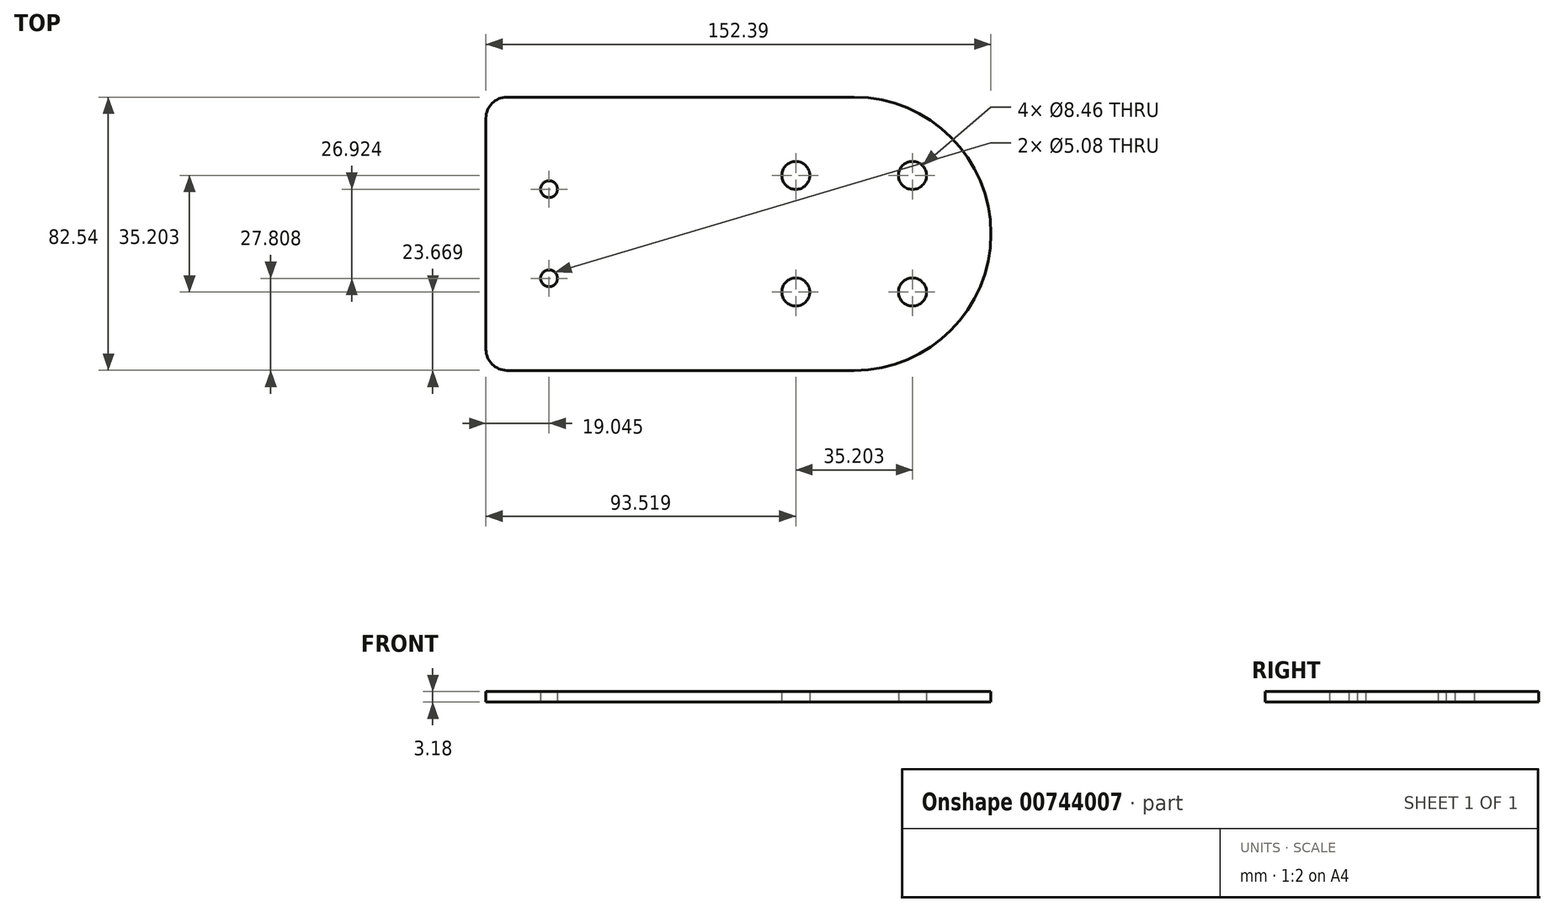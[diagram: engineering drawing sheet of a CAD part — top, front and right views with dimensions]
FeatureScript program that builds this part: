
annotation { "Feature Type Name" : "Feature", "Feature Type Description" : "" }
export const myFeature = defineFeature(function(context is Context, id is Id, definition is map)
    precondition{}
    {
        {
            var Q0;
            Q0=qCreatedBy(makeId("Top.planeOp"),FACE);
            var sketch = newSketch(context, id + "F0", { "sketchPlane" : qUnion([Q0])});
            skCircle(sketch, "E0", {"center": v(0, 0) * mm, "radius": 41.28 * mm});
            skLineSegment(sketch, "E1", {"start": v(-17.6, 17.6) * mm, "end": v(0, 0) * mm});
            skLineSegment(sketch, "E2", {"start": v(0, 2.83) * mm, "end": v(0, 41.28) * mm});
            skLineSegment(sketch, "E3.bottom", {"start": v(0, 41.28) * mm, "end": v(-104.78, 41.28) * mm});
            skLineSegment(sketch, "E3.top", {"start": v(0, -41.28) * mm, "end": v(-104.78, -41.28) * mm});
            skLineSegment(sketch, "E3.left", {"start": v(0, 41.28) * mm, "end": v(0, -41.28) * mm});
            skLineSegment(sketch, "E3.right", {"start": v(-111.13, 34.92) * mm, "end": v(-111.13, -34.92) * mm});
            skPoint(sketch, "E4.visualSharp", {"position": v(-111.13, -41.27) * mm});
            skArc(sketch, "E4.filletArc", {"start": v(-111.13, -34.92) * mm, "mid": v(-109.27, -39.42) * mm, "end": v(-104.78, -41.27) * mm});
            skPoint(sketch, "E5.visualSharp", {"position": v(-111.13, 41.27) * mm});
            skArc(sketch, "E5.filletArc", {"start": v(-104.78, 41.27) * mm, "mid": v(-109.27, 39.42) * mm, "end": v(-111.13, 34.92) * mm});
            skLineSegment(sketch, "E6", {"start": v(0, 0) * mm, "end": v(-111.13, 0) * mm});
            skCircle(sketch, "E7", {"center": v(-92.08, 13.46) * mm, "radius": 2.54 * mm});
            skCircle(sketch, "E8.0.1.0", {"center": v(-92.08, -13.46) * mm, "radius": 2.54 * mm});
            skLineSegment(sketch, "E8.direction1", {"start": v(-92.08, 13.46) * mm, "end": v(-66.68, 13.46) * mm, "construction": true});
            skLineSegment(sketch, "E8.direction2", {"start": v(-92.08, 13.46) * mm, "end": v(-92.08, -13.46) * mm, "construction": true});
            skLineSegment(sketch, "E9", {"start": v(17.6, 17.6) * mm, "end": v(0, 0) * mm});
            skLineSegment(sketch, "E10", {"start": v(-17.6, -17.6) * mm, "end": v(0, 0) * mm});
            skLineSegment(sketch, "E11", {"start": v(17.6, -17.6) * mm, "end": v(0, 0) * mm});
            skCircle(sketch, "E12", {"center": v(-17.6, 17.6) * mm, "radius": 4.23 * mm});
            skCircle(sketch, "E13", {"center": v(17.6, 17.6) * mm, "radius": 4.23 * mm});
            skCircle(sketch, "E14", {"center": v(17.6, -17.6) * mm, "radius": 4.23 * mm});
            skCircle(sketch, "E15", {"center": v(-17.6, -17.6) * mm, "radius": 4.23 * mm});
            skSolve(sketch);
        }
        {
            var Q0;
            {var subQ4=sQuery(id+"F0.wireOp",EDGE,"E3.bottom");Q0=makeQuery(id+"F0.imprint","IMPRINT",FACE,{"disambiguationData":[TD([[makeQuery(id+"F0.imprint","IMPRINT",EDGE,{"derivedFrom":subQ4}),1.0]])]});}
            var Q1;
            {var subQ4=sQuery(id+"F0.wireOp",EDGE,"E3.top");Q1=makeQuery(id+"F0.imprint","IMPRINT",FACE,{"disambiguationData":[TD([[makeQuery(id+"F0.imprint","IMPRINT",EDGE,{"derivedFrom":subQ4}),-1.0]])]});}
            var Q2;
            Q2=makeQuery(id+"F0.imprint","IMPRINT",FACE,{"disambiguationData":[TD([[makeQuery(id+"F0.imprint","IMPRINT",EDGE,{"derivedFrom":sQuery(id+"F0.wireOp",EDGE,"b3ae5090-ad33-4f2f-b20c-5e5ba8369b4a.1.0")}),-1.0]])]});
            var Q3;
            Q3=makeQuery(id+"F0.imprint","IMPRINT",FACE,{"disambiguationData":[TD([[makeQuery(id+"F0.imprint","IMPRINT",EDGE,{"derivedFrom":sQuery(id+"F0.wireOp",EDGE,"PXfZxHsB-QuWJ-UxBJ-qXLb-LhnyIbSCKvnw")}),-1.0]])]});
            var Q4;
            Q4=makeQuery(id+"F0.imprint","IMPRINT",FACE,{"disambiguationData":[TD([[makeQuery(id+"F0.imprint","IMPRINT",EDGE,{"derivedFrom":sQuery(id+"F0.wireOp",EDGE,"b3ae5090-ad33-4f2f-b20c-5e5ba8369b4a.2.0")}),-1.0]])]});
            var Q5;
            Q5=makeQuery(id+"F0.imprint","IMPRINT",FACE,{"disambiguationData":[TD([[makeQuery(id+"F0.imprint","IMPRINT",EDGE,{"derivedFrom":sQuery(id+"F0.wireOp",EDGE,"E12")}),-1.0]])]});
            var Q6;
            Q6=makeQuery(id+"F0.imprint","IMPRINT",FACE,{"disambiguationData":[TD([[makeQuery(id+"F0.imprint","IMPRINT",EDGE,{"derivedFrom":sQuery(id+"F0.wireOp",EDGE,"E15")}),-1.0]])]});
            var Q7;
            Q7=makeQuery(id+"F0.imprint","IMPRINT",FACE,{"disambiguationData":[TD([[makeQuery(id+"F0.imprint","IMPRINT",EDGE,{"derivedFrom":sQuery(id+"F0.wireOp",EDGE,"E13")}),-1.0]])]});
            extrude(context, id + "F1", {"entities" : qUnion([Q0, Q1, Q2, Q3, Q4, Q5, Q6, Q7]), "depth" : 3.17 * mm, "offsetDistance" : 25.4 * mm});
        }
    });
